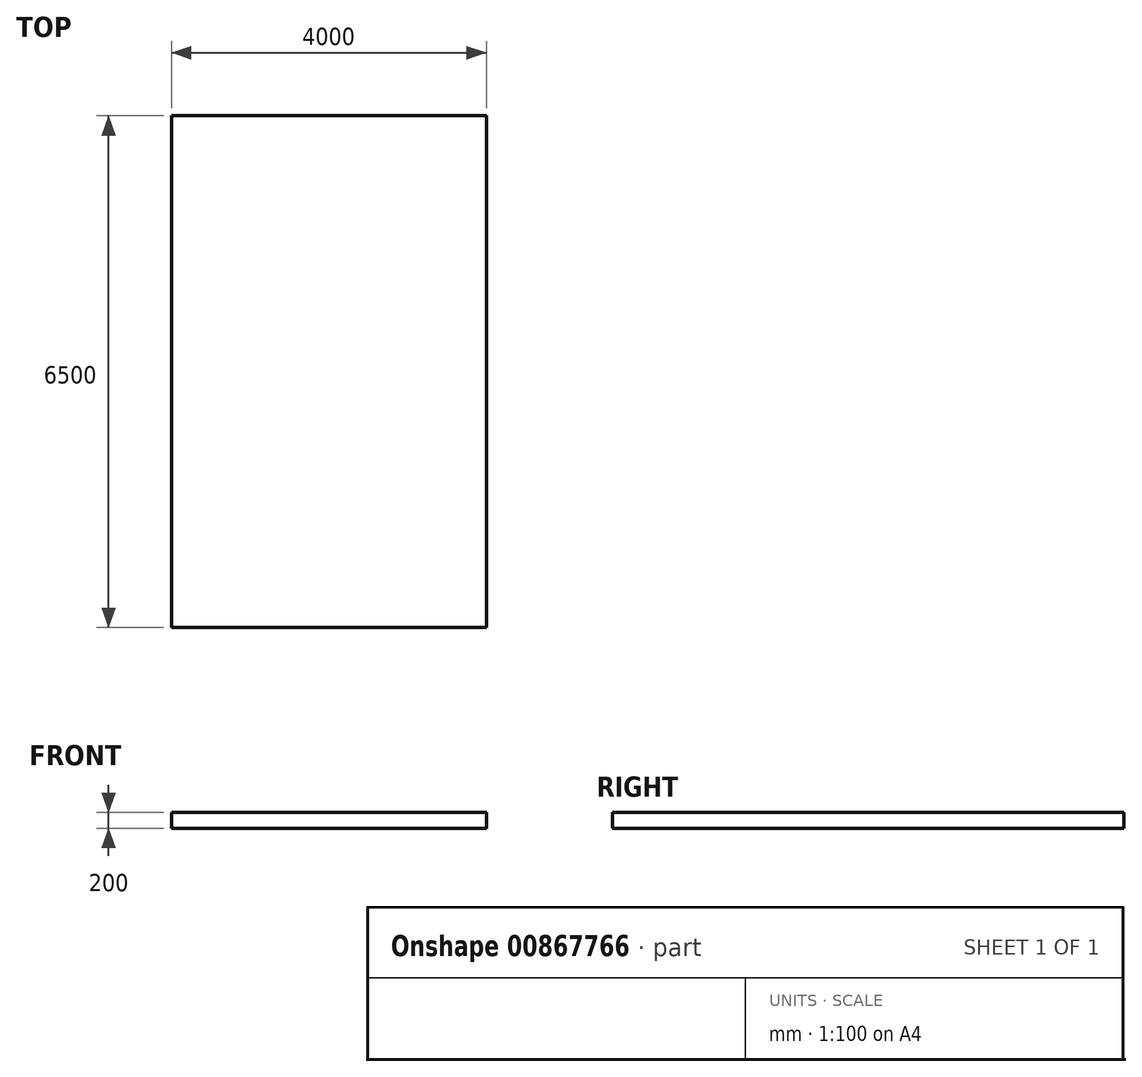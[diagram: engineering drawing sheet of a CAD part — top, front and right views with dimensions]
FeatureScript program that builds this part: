
annotation { "Feature Type Name" : "Feature", "Feature Type Description" : "" }
export const myFeature = defineFeature(function(context is Context, id is Id, definition is map)
    precondition{}
    {
        {
            var Q0;
            Q0=qCreatedBy(makeId("Top.planeOp"),FACE);
            var sketch = newSketch(context, id + "F0", { "sketchPlane" : qUnion([Q0])});
            skLineSegment(sketch, "E0.bottom", {"start": v(2000, -3250) * mm, "end": v(-2000, -3250) * mm});
            skLineSegment(sketch, "E0.top", {"start": v(2000, 3250) * mm, "end": v(-2000, 3250) * mm});
            skLineSegment(sketch, "E0.left", {"start": v(2000, -3250) * mm, "end": v(2000, 3250) * mm});
            skLineSegment(sketch, "E0.right", {"start": v(-2000, -3250) * mm, "end": v(-2000, 3250) * mm});
            skPoint(sketch, "E0.middle", {"position": v(0, 0) * mm});
            skSolve(sketch);
        }
        {
            var Q0;
            Q0=makeQuery(id+"F0.imprint","IMPRINT",FACE,{"disambiguationData":[TD([[makeQuery(id+"F0.imprint","IMPRINT",EDGE,{"derivedFrom":sQuery(id+"F0.wireOp",EDGE,"E0.bottom")}),-1.0]])]});
            extrude(context, id + "F1", {"entities" : qUnion([Q0]), "depth" : 200 * mm, "offsetDistance" : 25 * mm});
        }
    });
